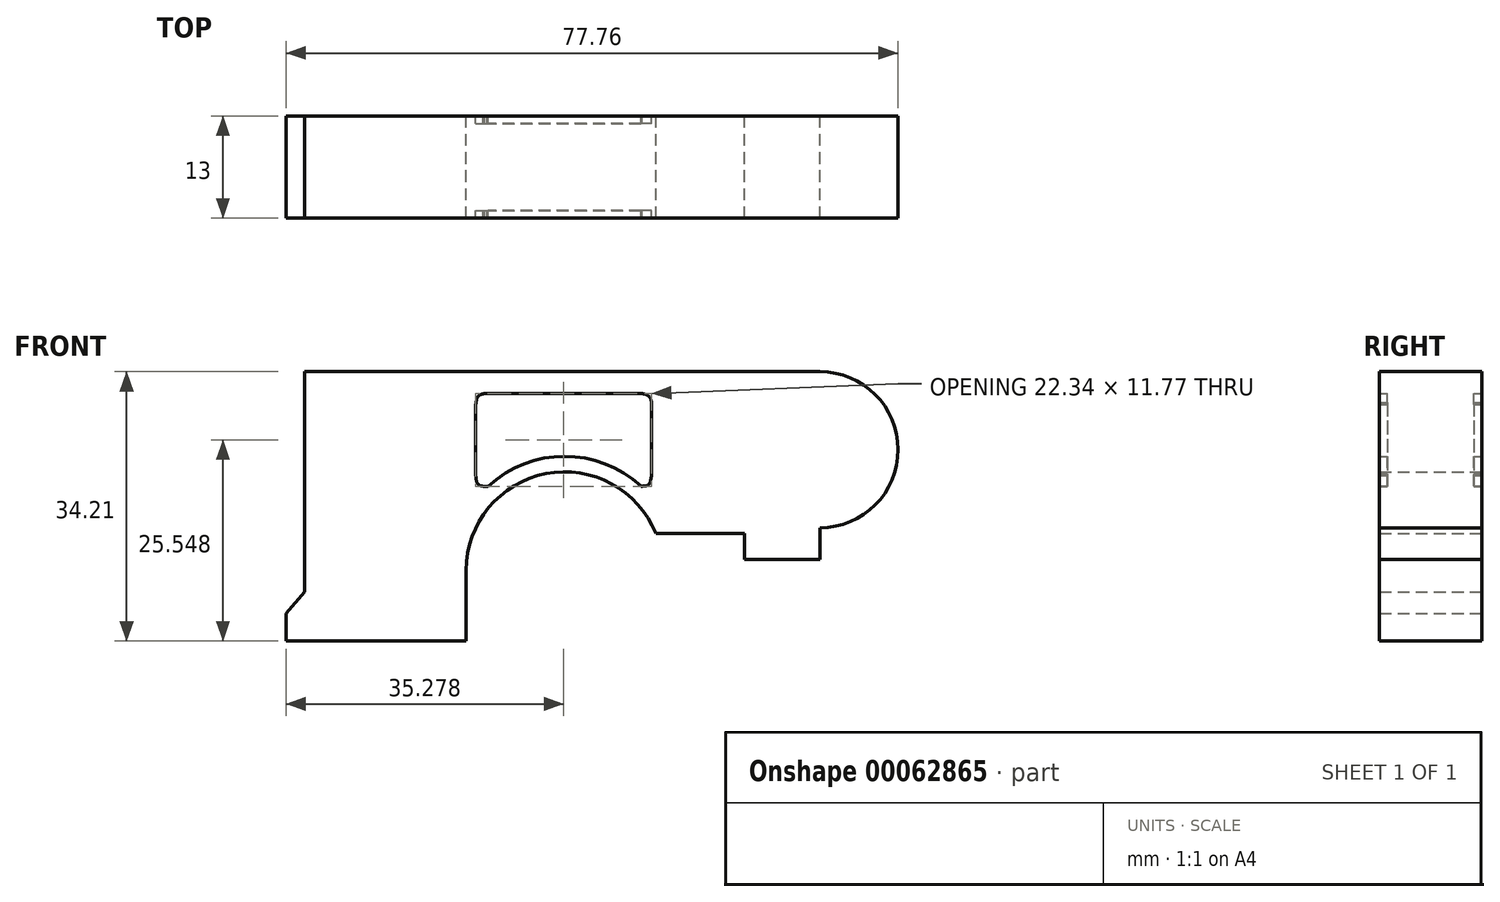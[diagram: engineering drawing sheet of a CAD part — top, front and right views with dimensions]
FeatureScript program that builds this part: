
annotation { "Feature Type Name" : "Feature", "Feature Type Description" : "" }
export const myFeature = defineFeature(function(context is Context, id is Id, definition is map)
    precondition{}
    {
        {
            var Q0;
            Q0=qCreatedBy(makeId("Front.planeOp"),FACE);
            var sketch = newSketch(context, id + "F0", { "sketchPlane" : qUnion([Q0])});
            skLineSegment(sketch, "E0", {"start": v(-35.4, 0) * mm, "end": v(0, 0) * mm});
            skLineSegment(sketch, "E1", {"start": v(-35.4, 0) * mm, "end": v(-35.4, 7.02) * mm});
            skLineSegment(sketch, "E2", {"start": v(-33.05, 9.74) * mm, "end": v(-35.4, 7.02) * mm});
            skLineSegment(sketch, "E3", {"start": v(-33.05, 9.74) * mm, "end": v(-33.05, 37.72) * mm});
            skLineSegment(sketch, "E4", {"start": v(-33.05, 37.72) * mm, "end": v(32.45, 37.72) * mm});
            skLineSegment(sketch, "E5", {"start": v(32.45, 37.72) * mm, "end": v(32.45, -10) * mm});
            skCircle(sketch, "E6", {"center": v(32.45, 27.81) * mm, "radius": 9.91 * mm});
            skLineSegment(sketch, "E7", {"start": v(32.45, 25) * mm, "end": v(-19.87, 25) * mm});
            skLineSegment(sketch, "E8", {"start": v(0, 25) * mm, "end": v(0, 5.92) * mm});
            skCircle(sketch, "E9", {"center": v(0, 12.5) * mm, "radius": 12.5 * mm});
            skLineSegment(sketch, "E10", {"start": v(-35.4, 0) * mm, "end": v(62.5, 0) * mm});
            skLineSegment(sketch, "E11", {"start": v(0, 5.92) * mm, "end": v(0, 0) * mm});
            skLineSegment(sketch, "E12", {"start": v(0, 0) * mm, "end": v(32.45, 0) * mm});
            skLineSegment(sketch, "E13", {"start": v(32.45, 13.86) * mm, "end": v(22.83, 13.86) * mm});
            skLineSegment(sketch, "E14", {"start": v(22.83, 13.86) * mm, "end": v(22.83, 17.17) * mm});
            skLineSegment(sketch, "E15", {"start": v(22.83, 17.17) * mm, "end": v(11.6, 17.17) * mm});
            skLineSegment(sketch, "E16", {"start": v(0, 12.5) * mm, "end": v(12.5, 12.5) * mm});
            skLineSegment(sketch, "E17", {"start": v(0, 12.5) * mm, "end": v(-12.5, 12.5) * mm});
            skLineSegment(sketch, "E18", {"start": v(-35.4, 7.02) * mm, "end": v(-35.4, 3.51) * mm});
            skPoint(sketch, "E18.endSnap0", {"position": v(-35.4, 3.51) * mm});
            skLineSegment(sketch, "E19", {"start": v(-35.4, 3.51) * mm, "end": v(-8.69, 3.51) * mm});
            skLineSegment(sketch, "E20", {"start": v(-12.5, 12.5) * mm, "end": v(-12.5, 0) * mm});
            skSolve(sketch);
        }
        {
            var Q0;
            Q0=makeQuery(id+"F0.imprint","IMPRINT",FACE,{"disambiguationData":[TD([[makeQuery(id+"F0.imprint","IMPRINT",EDGE,{"derivedFrom":sQuery(id+"F0.wireOp",EDGE,"E2")}),1.0]])]});
            var Q1;
            {var subQ1=sQuery(id+"F0.wireOp",EDGE,"E5");var subQ3=sQuery(id+"F0.wireOp",EDGE,"E7");var subQ4=makeQuery(id+"F0.imprint","INTERSECT",VERTEX,{"derivedFrom":[subQ1,subQ3]});Q1=makeQuery(id+"F0.imprint","IMPRINT",FACE,{"disambiguationData":[TD([[makeQuery(id+"F0.imprint","IMPRINT",EDGE,{"disambiguationData":[TD([[subQ4,-1.0]])],"derivedFrom":subQ3}),-1.0]])]});}
            var Q2;
            {var subQ1=sQuery(id+"F0.wireOp",EDGE,"E5");var subQ3=makeQuery(id+"F0.imprint","INTERSECT",VERTEX,{"derivedFrom":[subQ1,sQuery(id+"F0.wireOp",EDGE,"E7")]});Q2=makeQuery(id+"F0.imprint","IMPRINT",FACE,{"disambiguationData":[TD([[makeQuery(id+"F0.imprint","IMPRINT",EDGE,{"disambiguationData":[TD([[subQ3,-1.0]])],"derivedFrom":subQ1}),1.0]])]});}
            var Q3;
            {var subQ0=sQuery(id+"F0.wireOp",EDGE,"E7");var subQ1=sQuery(id+"F0.wireOp",EDGE,"E5");var subQ2=makeQuery(id+"F0.imprint","INTERSECT",VERTEX,{"derivedFrom":[subQ1,subQ0]});Q3=makeQuery(id+"F0.imprint","IMPRINT",FACE,{"disambiguationData":[TD([[makeQuery(id+"F0.imprint","IMPRINT",EDGE,{"disambiguationData":[TD([[subQ2,-1.0]])],"derivedFrom":subQ1}),-1.0]])]});}
            var Q4;
            {var subQ8=sQuery(id+"F0.wireOp",EDGE,"E13");Q4=makeQuery(id+"F0.imprint","IMPRINT",FACE,{"disambiguationData":[TD([[makeQuery(id+"F0.imprint","IMPRINT",EDGE,{"derivedFrom":subQ8}),-1.0]])]});}
            extrude(context, id + "F1", {"entities" : qUnion([Q0, Q1, Q2, Q3, Q4]), "depth" : 13 * mm});
        }
        {
            var Q0;
            Q0=qCreatedBy(makeId("Front.planeOp"),FACE);
            var sketch = newSketch(context, id + "F2", { "sketchPlane" : qUnion([Q0])});
            skCircle(sketch, "E21", {"center": v(0, 12.72) * mm, "radius": 12.34 * mm});
            skPoint(sketch, "E21.first.point", {"position": v(0, 25.07) * mm});
            skPoint(sketch, "E21.second.point", {"position": v(-11.42, 17.4) * mm});
            skPoint(sketch, "E21.third.point", {"position": v(11.38, 17.5) * mm});
            skCircle(sketch, "E22", {"center": v(0, 12.72) * mm, "radius": 14.25 * mm});
            skLineSegment(sketch, "E23.bottom", {"start": v(-11.29, 34.94) * mm, "end": v(11.05, 34.94) * mm});
            skLineSegment(sketch, "E23.top", {"start": v(-11.29, 23.17) * mm, "end": v(11.05, 23.17) * mm});
            skLineSegment(sketch, "E23.left", {"start": v(-11.29, 34.94) * mm, "end": v(-11.29, 23.17) * mm});
            skLineSegment(sketch, "E23.right", {"start": v(11.05, 34.94) * mm, "end": v(11.05, 23.17) * mm});
            skLineSegment(sketch, "E24", {"start": v(-10.17, 34.94) * mm, "end": v(-11.29, 33.55) * mm});
            skFitSpline(sketch, "E25", {"points": [v(-11.29, 33.55) * mm, v(-10.97, 34.6) * mm, v(-10.17, 34.94) * mm], "startDerivative": vector(0.32, 2.33) * mm, "endDerivative": vector(1.95, 0.41) * mm});
            skLineSegment(sketch, "E26", {"start": v(-9.7, 23.17) * mm, "end": v(-11.29, 24.57) * mm});
            skFitSpline(sketch, "E27", {"points": [v(-11.29, 24.57) * mm, v(-10.92, 23.35) * mm, v(-9.7, 23.17) * mm], "startDerivative": vector(0.3, -2.14) * mm, "endDerivative": vector(1.82, -0.06) * mm});
            skLineSegment(sketch, "E28", {"start": v(9.84, 34.94) * mm, "end": v(11.05, 33.8) * mm});
            skFitSpline(sketch, "E29", {"points": [v(11.05, 33.8) * mm, v(10.73, 34.6) * mm, v(9.84, 34.94) * mm], "startDerivative": vector(-0.38, 1.87) * mm, "endDerivative": vector(-2.02, 0.42) * mm});
            skLineSegment(sketch, "E30", {"start": v(11.05, 24.76) * mm, "end": v(9.68, 23.17) * mm});
            skFitSpline(sketch, "E31", {"points": [v(11.05, 24.76) * mm, v(10.75, 23.47) * mm, v(9.68, 23.17) * mm], "startDerivative": vector(-0.32, -2.43) * mm, "endDerivative": vector(-2.8, 0) * mm});
            skSolve(sketch);
        }
        {
            var Q0;
            {var subQ10=sQuery(id+"F2.wireOp",EDGE,"E24");Q0=makeQuery(id+"F2.imprint","IMPRINT",FACE,{"disambiguationData":[TD([[makeQuery(id+"F2.imprint","IMPRINT",EDGE,{"derivedFrom":subQ10}),1.0]])]});}
            var Q1;
            Q1=makeQuery(id+"F2.imprint","IMPRINT",FACE,{"disambiguationData":[TD([[makeQuery(id+"F2.imprint","IMPRINT",EDGE,{"derivedFrom":sQuery(id+"F2.wireOp",EDGE,"E24")}),-1.0]])]});
            var Q2;
            Q2=makeQuery(id+"F2.imprint","IMPRINT",FACE,{"disambiguationData":[TD([[makeQuery(id+"F2.imprint","IMPRINT",EDGE,{"derivedFrom":sQuery(id+"F2.wireOp",EDGE,"E28")}),1.0]])]});
            var Q3;
            Q3=makeQuery(id+"F2.imprint","IMPRINT",FACE,{"disambiguationData":[TD([[makeQuery(id+"F2.imprint","IMPRINT",EDGE,{"derivedFrom":sQuery(id+"F2.wireOp",EDGE,"E30")}),1.0]])]});
            var Q4;
            {var subQ0=sQuery(id+"F2.wireOp",EDGE,"E27");Q4=makeQuery(id+"F2.imprint","IMPRINT",FACE,{"disambiguationData":[TD([[makeQuery(id+"F2.imprint","IMPRINT",EDGE,{"derivedFrom":subQ0}),1.0]])]});}
            extrude(context, id + "F3", {"entities" : qUnion([Q0, Q1, Q2, Q3, Q4]), "depth" : 2 * mm});
        }
        {
            var Q0;
            Q0=makeQuery(id+"F3.opExtrude","SWEPT_BODY",BODY,{"disambiguationData":[OSD([sQuery(id+"F2.wireOp",EDGE,"E22"),sQuery(id+"F2.wireOp",EDGE,"E23.bottom"),sQuery(id+"F2.wireOp",EDGE,"E23.top"),sQuery(id+"F2.wireOp",EDGE,"E23.left"),sQuery(id+"F2.wireOp",EDGE,"E23.right"),sQuery(id+"F2.wireOp",EDGE,"E24"),sQuery(id+"F2.wireOp",EDGE,"E26"),sQuery(id+"F2.wireOp",EDGE,"E28"),sQuery(id+"F2.wireOp",EDGE,"E30")])]});
            transform(context, id + "F4", {"entities" : qUnion([Q0]), "transformType" : TransformType.TRANSLATION_3D, "dx" : 0 * mm, "dy" : 1 * mm, "dz" : 0 * mm, "makeCopy" : false});
        }
        {
            var Q0;
            Q0=makeQuery(id+"F3.opExtrude","SWEPT_BODY",BODY,{"disambiguationData":[OSD([sQuery(id+"F2.wireOp",EDGE,"E22"),sQuery(id+"F2.wireOp",EDGE,"E23.bottom"),sQuery(id+"F2.wireOp",EDGE,"E23.top"),sQuery(id+"F2.wireOp",EDGE,"E23.left"),sQuery(id+"F2.wireOp",EDGE,"E23.right"),sQuery(id+"F2.wireOp",EDGE,"E24"),sQuery(id+"F2.wireOp",EDGE,"E26"),sQuery(id+"F2.wireOp",EDGE,"E28"),sQuery(id+"F2.wireOp",EDGE,"E30")])]});
            var Q1;
            Q1=makeQuery(id+"F1.opExtrude","SWEPT_BODY",BODY,{"disambiguationData":[OSD([sQuery(id+"F0.wireOp",EDGE,"E2"),sQuery(id+"F0.wireOp",EDGE,"E3"),sQuery(id+"F0.wireOp",EDGE,"E4"),sQuery(id+"F0.wireOp",EDGE,"E5"),sQuery(id+"F0.wireOp",EDGE,"E6"),sQuery(id+"F0.wireOp",EDGE,"E9"),sQuery(id+"F0.wireOp",EDGE,"E13"),sQuery(id+"F0.wireOp",EDGE,"E14"),sQuery(id+"F0.wireOp",EDGE,"E15"),sQuery(id+"F0.wireOp",EDGE,"E18"),sQuery(id+"F0.wireOp",EDGE,"E19"),sQuery(id+"F0.wireOp",EDGE,"E20")])]});
            booleanBodies(context, id + "F5", {"operationType" : BooleanOperationType.SUBTRACTION, "tools" : qUnion([Q0]), "targets" : qUnion([Q1]), "keepTools" : true});
        }
        {
            var Q0;
            Q0=makeQuery(id+"F3.opExtrude","SWEPT_BODY",BODY,{"disambiguationData":[OSD([sQuery(id+"F2.wireOp",EDGE,"E22"),sQuery(id+"F2.wireOp",EDGE,"E23.bottom"),sQuery(id+"F2.wireOp",EDGE,"E23.top"),sQuery(id+"F2.wireOp",EDGE,"E23.left"),sQuery(id+"F2.wireOp",EDGE,"E23.right"),sQuery(id+"F2.wireOp",EDGE,"E24"),sQuery(id+"F2.wireOp",EDGE,"E26"),sQuery(id+"F2.wireOp",EDGE,"E28"),sQuery(id+"F2.wireOp",EDGE,"E30")])]});
            transform(context, id + "F6", {"entities" : qUnion([Q0]), "transformType" : TransformType.TRANSLATION_3D, "dx" : 0 * mm, "dy" : -13 * mm, "dz" : 0 * mm, "makeCopy" : false});
        }
        {
            var Q0;
            Q0=makeQuery(id+"F3.opExtrude","SWEPT_BODY",BODY,{"disambiguationData":[OSD([sQuery(id+"F2.wireOp",EDGE,"E22"),sQuery(id+"F2.wireOp",EDGE,"E23.bottom"),sQuery(id+"F2.wireOp",EDGE,"E23.top"),sQuery(id+"F2.wireOp",EDGE,"E23.left"),sQuery(id+"F2.wireOp",EDGE,"E23.right"),sQuery(id+"F2.wireOp",EDGE,"E24"),sQuery(id+"F2.wireOp",EDGE,"E26"),sQuery(id+"F2.wireOp",EDGE,"E28"),sQuery(id+"F2.wireOp",EDGE,"E30")])]});
            var Q1;
            Q1=makeQuery(id+"F1.opExtrude","SWEPT_BODY",BODY,{"disambiguationData":[OSD([sQuery(id+"F0.wireOp",EDGE,"E2"),sQuery(id+"F0.wireOp",EDGE,"E3"),sQuery(id+"F0.wireOp",EDGE,"E4"),sQuery(id+"F0.wireOp",EDGE,"E5"),sQuery(id+"F0.wireOp",EDGE,"E6"),sQuery(id+"F0.wireOp",EDGE,"E9"),sQuery(id+"F0.wireOp",EDGE,"E13"),sQuery(id+"F0.wireOp",EDGE,"E14"),sQuery(id+"F0.wireOp",EDGE,"E15"),sQuery(id+"F0.wireOp",EDGE,"E18"),sQuery(id+"F0.wireOp",EDGE,"E19"),sQuery(id+"F0.wireOp",EDGE,"E20")])]});
            booleanBodies(context, id + "F7", {"operationType" : BooleanOperationType.SUBTRACTION, "tools" : qUnion([Q0]), "targets" : qUnion([Q1])});
        }
    });
